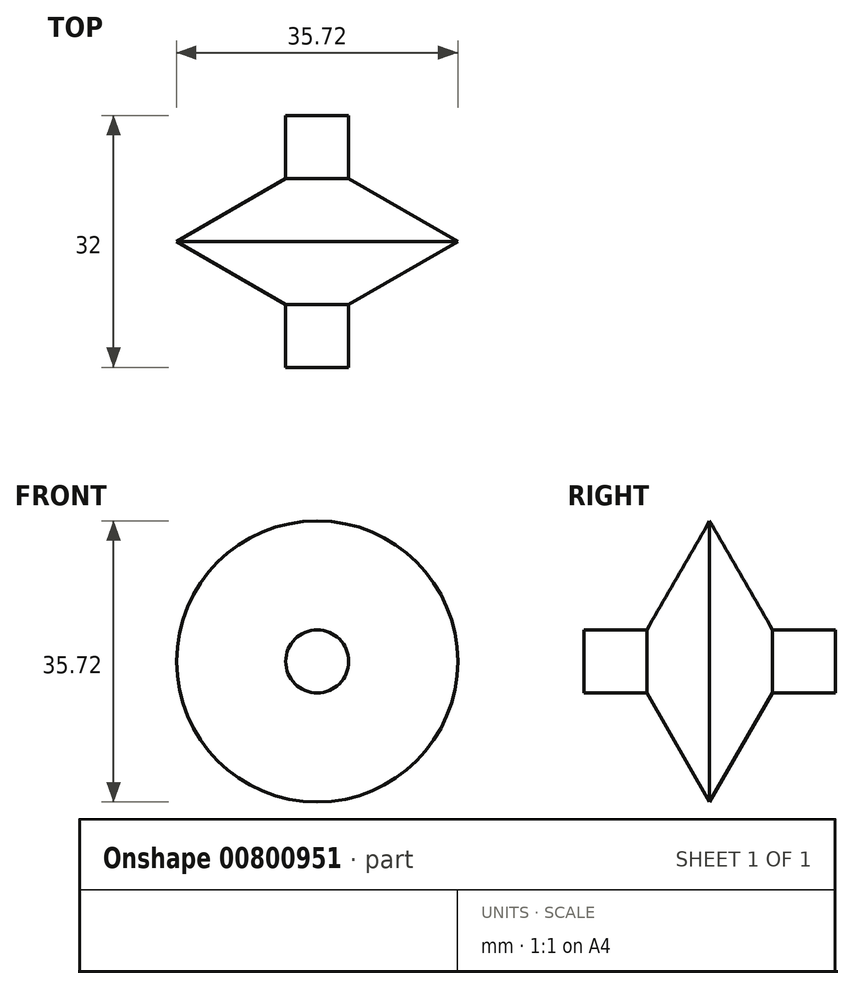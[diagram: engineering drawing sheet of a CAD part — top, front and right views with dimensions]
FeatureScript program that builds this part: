
annotation { "Feature Type Name" : "Feature", "Feature Type Description" : "" }
export const myFeature = defineFeature(function(context is Context, id is Id, definition is map)
    precondition{}
    {
        {
            var Q0;
            Q0=qCreatedBy(makeId("Top.planeOp"),FACE);
            var sketch = newSketch(context, id + "F0", { "sketchPlane" : qUnion([Q0])});
            skLineSegment(sketch, "E0", {"start": v(0, 0) * mm, "end": v(0, -32) * mm});
            skLineSegment(sketch, "E1", {"start": v(0, -32) * mm, "end": v(4, -32) * mm});
            skLineSegment(sketch, "E2", {"start": v(4, -32) * mm, "end": v(4, -24) * mm});
            skLineSegment(sketch, "E3", {"start": v(4, -24) * mm, "end": v(17.86, -16) * mm});
            skLineSegment(sketch, "E4", {"start": v(17.86, -16) * mm, "end": v(4, -8) * mm});
            skLineSegment(sketch, "E5", {"start": v(4, -8) * mm, "end": v(4, 0) * mm});
            skLineSegment(sketch, "E6", {"start": v(4, 0) * mm, "end": v(0, 0) * mm});
            skLineSegment(sketch, "E7", {"start": v(4, -12.62) * mm, "end": v(4, -19.38) * mm});
            skLineSegment(sketch, "E8", {"start": v(4, -19.38) * mm, "end": v(9.86, -16) * mm});
            skLineSegment(sketch, "E9", {"start": v(9.86, -16) * mm, "end": v(4, -12.62) * mm});
            skSolve(sketch);
        }
        {
            var Q0;
            Q0=makeQuery(id+"F0.imprint","IMPRINT",FACE,{"disambiguationData":[TD([[makeQuery(id+"F0.imprint","IMPRINT",EDGE,{"derivedFrom":sQuery(id+"F0.wireOp",EDGE,"E0")}),1.0]])]});
            var Q1;
            Q1=makeQuery(id+"F0.imprint","IMPRINT",FACE,{"disambiguationData":[TD([[makeQuery(id+"F0.imprint","IMPRINT",EDGE,{"derivedFrom":sQuery(id+"F0.wireOp",EDGE,"E7")}),1.0]])]});
            var Q2;
            Q2=sQuery(id+"F0.wireOp",EDGE,"E0");
            revolve(context, id + "F1", {"surfaceOperationType" : NewSurfaceOperationType.NEW, "entities" : qUnion([Q0, Q1]), "axis" : qUnion([Q2]), "revolveType" : RevolveType.FULL});
        }
    });
